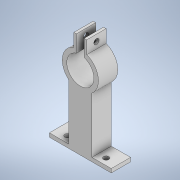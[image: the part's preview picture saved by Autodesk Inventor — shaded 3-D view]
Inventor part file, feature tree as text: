
AUTODESK INVENTOR PART (.ipt)
format: ipt  version: 2022 (Build 260153000, 153)  size: 164,864 bytes
history: native  units: mm
features: extrude x4, sketch x4, reference x4, other x3, plane x2
ambient origin geometry x8: Origin, YZ Plane, XZ Plane, XY Plane, X Axis, Y Axis, Z Axis, Center Point
bodies: Body1 (feature_tree)
feature tree (17):
  plane  "Work Plane3"
  extrude  "Extrusion2"  Depth=2.5mm
  extrude  "Extrusion4"  Depth=15.0mm
  plane  "Work Plane5"
  extrude  "Extrusion5"  Depth=48.0mm
  extrude  "Extrusion6"  Depth=10.0mm
  sketch  "Sketch3"  dims[d8=0.0mm d9=2.5mm]
  reference  "Reference3"
  sketch  "Sketch5"  dims[d13=14.0mm d14=15.0mm d15=0.0mm d19=9.0mm]
  reference  "Reference4"
  sketch  "Sketch7"  dims[d20=15.0mm d21=0.0mm d23=48.0mm]
  reference  "Reference5"
  reference  "Reference6"
  sketch  "Sketch8"  dims[d24=15.0mm d25=9.0mm d26=3.0mm d27=0.0mm d28=2.0mm d30=10.0mm d31=2.0mm d32=3.0mm d33=14.0mm d34=4.0mm d35=10.0mm d36=0.0mm]
  other  "Assembly_Final.iam"
  other  "motor:1"
  other  "Base_proyecto:1"
